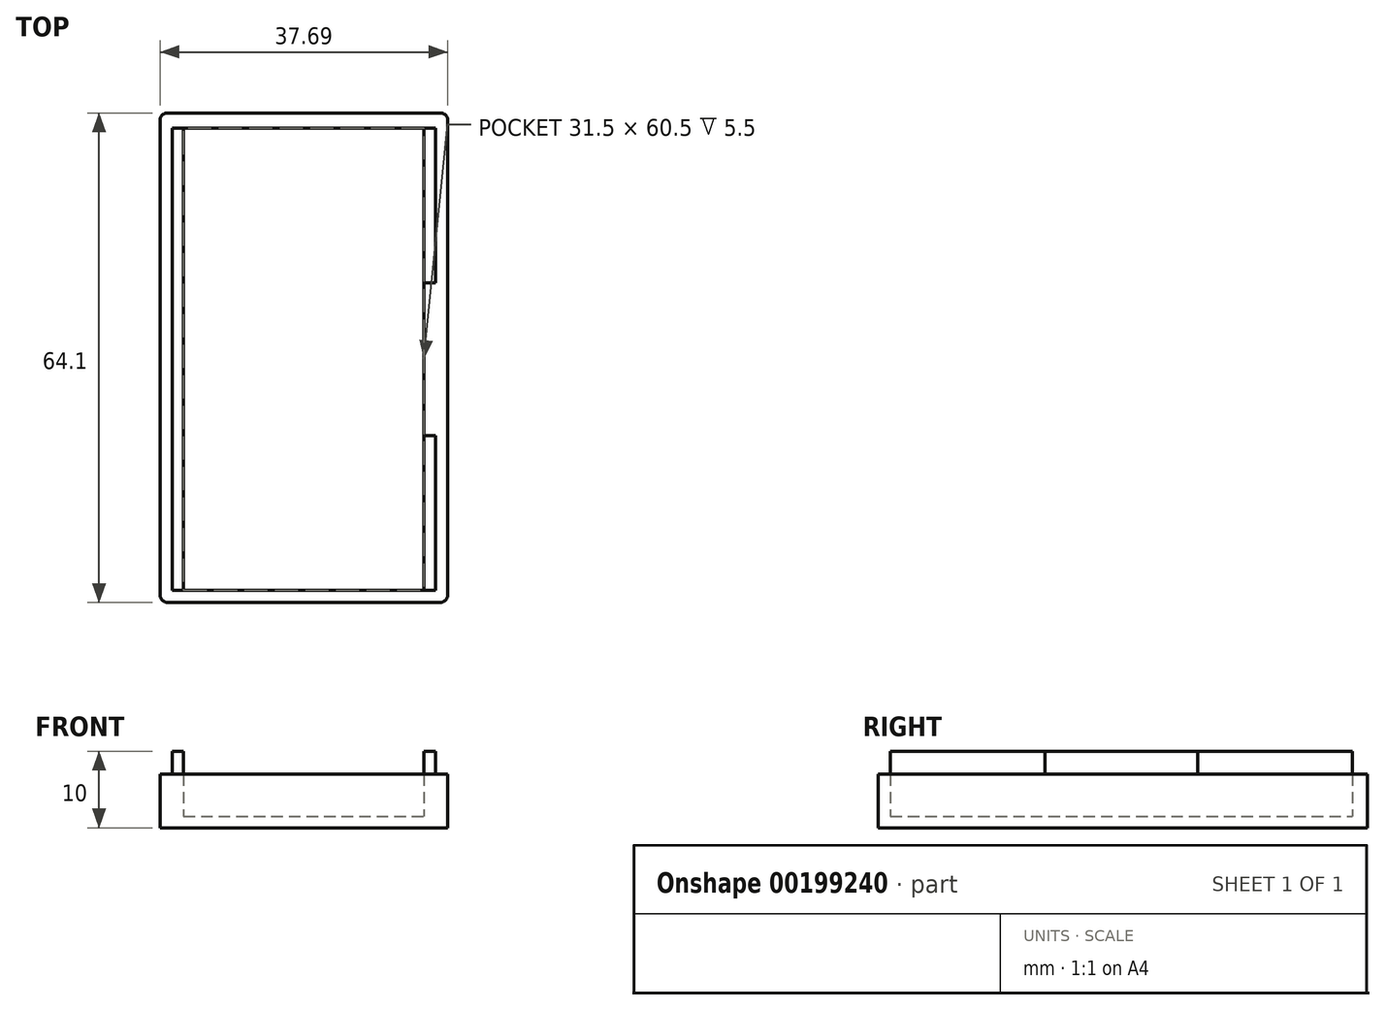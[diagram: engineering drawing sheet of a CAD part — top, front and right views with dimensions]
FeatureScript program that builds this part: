
annotation { "Feature Type Name" : "Feature", "Feature Type Description" : "" }
export const myFeature = defineFeature(function(context is Context, id is Id, definition is map)
    precondition{}
    {
        {
            var Q0;
            Q0=qCreatedBy(makeId("Top.planeOp"),FACE);
            var sketch = newSketch(context, id + "F0", { "sketchPlane" : qUnion([Q0])});
            skLineSegment(sketch, "E0.0.0", {"start": v(18.85, 32.25) * mm, "end": v(-18.84, 32.25) * mm});
            skLineSegment(sketch, "E0.0.1", {"start": v(-18.84, 32.25) * mm, "end": v(-18.84, -31.85) * mm});
            skLineSegment(sketch, "E0.0.2", {"start": v(-18.84, -31.85) * mm, "end": v(18.85, -31.85) * mm});
            skLineSegment(sketch, "E0.0.3", {"start": v(18.85, -31.85) * mm, "end": v(18.85, 32.25) * mm});
            skLineSegment(sketch, "E1.0", {"start": v(-15.75, 30.25) * mm, "end": v(15.75, 30.25) * mm});
            skLineSegment(sketch, "E2.0", {"start": v(-15.75, -30.25) * mm, "end": v(-15.75, 30.25) * mm});
            skLineSegment(sketch, "E3.0", {"start": v(15.75, -30.25) * mm, "end": v(15.75, 30.25) * mm});
            skLineSegment(sketch, "E4.0", {"start": v(-15.75, -30.25) * mm, "end": v(15.75, -30.25) * mm});
            skPoint(sketch, "E5", {"position": v(0, 0) * mm});
            skPoint(sketch, "E5.positionSnap0", {"position": v(0, -30.25) * mm});
            skPoint(sketch, "E6.positionSnap0", {"position": v(15.75, 0) * mm});
            skSolve(sketch);
        }
        {
            var Q0;
            Q0 = qSketchRegion(id + "F0", true);
            extrude(context, id + "F1", {"entities" : qUnion([Q0]), "depth" : 7 * mm});
        }
        {
            var Q0;
            Q0=makeQuery(id+"F0.imprint","IMPRINT",FACE,{"disambiguationData":[TD([[makeQuery(id+"F0.imprint","IMPRINT",EDGE,{"derivedFrom":sQuery(id+"F0.wireOp",EDGE,"E1.0")}),-1.0]])]});
            extrude(context, id + "F2", {"entities" : qUnion([Q0]), "operationType" : NewBodyOperationType.ADD, "depth" : 1.5 * mm});
        }
        {
            var Q0;
            Q0=makeQuery(id+"F1.opExtrude","CAP_FACE",FACE,{"disambiguationData":[OSD([sQuery(id+"F0.wireOp",EDGE,"E0.0.0"),sQuery(id+"F0.wireOp",EDGE,"E0.0.1"),sQuery(id+"F0.wireOp",EDGE,"E0.0.2"),sQuery(id+"F0.wireOp",EDGE,"E0.0.3"),sQuery(id+"F0.wireOp",EDGE,"E1.0"),sQuery(id+"F0.wireOp",EDGE,"E2.0"),sQuery(id+"F0.wireOp",EDGE,"E3.0"),sQuery(id+"F0.wireOp",EDGE,"E4.0")])],"isStart":false});
            var sketch = newSketch(context, id + "F3", { "sketchPlane" : qUnion([Q0])});
            skLineSegment(sketch, "E7.0", {"start": v(-15.75, -30.25) * mm, "end": v(-15.75, 30.25) * mm});
            skLineSegment(sketch, "E8.0", {"start": v(15.75, -30.25) * mm, "end": v(15.75, 30.25) * mm});
            skLineSegment(sketch, "E9", {"start": v(-15.75, 30.25) * mm, "end": v(-17.25, 30.25) * mm});
            skLineSegment(sketch, "E10", {"start": v(-17.25, 30.25) * mm, "end": v(-17.25, -30.25) * mm});
            skLineSegment(sketch, "E11", {"start": v(-17.25, -30.25) * mm, "end": v(-15.75, -30.25) * mm});
            skLineSegment(sketch, "E12", {"start": v(15.75, -30.25) * mm, "end": v(17.25, -30.25) * mm});
            skLineSegment(sketch, "E13", {"start": v(17.25, -30.25) * mm, "end": v(17.25, 30.25) * mm});
            skLineSegment(sketch, "E14", {"start": v(17.25, 30.25) * mm, "end": v(15.75, 30.25) * mm});
            skSolve(sketch);
        }
        {
            var Q0;
            Q0 = qSketchRegion(id + "F3", true);
            extrude(context, id + "F4", {"entities" : qUnion([Q0]), "operationType" : NewBodyOperationType.ADD, "depth" : 3 * mm});
        }
        {
            var Q0;
            Q0=makeQuery(id+"F1.opExtrude","SWEPT_EDGE",EDGE,{"disambiguationData":[OSD([sQuery(id+"F0.wireOp",EDGE,"E0.0.1"),sQuery(id+"F0.wireOp",EDGE,"E0.0.2")])]});
            var Q1;
            Q1=makeQuery(id+"F1.opExtrude","SWEPT_EDGE",EDGE,{"disambiguationData":[OSD([sQuery(id+"F0.wireOp",EDGE,"E0.0.2"),sQuery(id+"F0.wireOp",EDGE,"E0.0.3")])]});
            var Q2;
            Q2=makeQuery(id+"F1.opExtrude","SWEPT_EDGE",EDGE,{"disambiguationData":[OSD([sQuery(id+"F0.wireOp",EDGE,"E0.0.0"),sQuery(id+"F0.wireOp",EDGE,"E0.0.3")])]});
            var Q3;
            Q3=makeQuery(id+"F1.opExtrude","SWEPT_EDGE",EDGE,{"disambiguationData":[OSD([sQuery(id+"F0.wireOp",EDGE,"E0.0.0"),sQuery(id+"F0.wireOp",EDGE,"E0.0.1")])]});
            fillet(context, id + "F5", {"entities" : qUnion([Q0, Q1, Q2, Q3]), "radius" : 1 * mm, "tangentPropagation" : true, "allowEdgeOverflow" : false});
        }
        {
            var Q0;
            Q0=makeQuery(id+"F4.opExtrude","SWEPT_FACE",FACE,{"disambiguationData":[OSD([sQuery(id+"F3.wireOp",EDGE,"E13")])]});
            var sketch = newSketch(context, id + "F6", { "sketchPlane" : qUnion([Q0])});
            skLineSegment(sketch, "E15.bottom", {"start": v(10, 7) * mm, "end": v(-10, 7) * mm});
            skLineSegment(sketch, "E15.top", {"start": v(10, 10) * mm, "end": v(-10, 10) * mm});
            skLineSegment(sketch, "E15.left", {"start": v(10, 7) * mm, "end": v(10, 10) * mm});
            skLineSegment(sketch, "E15.right", {"start": v(-10, 7) * mm, "end": v(-10, 10) * mm});
            skPoint(sketch, "E16", {"position": v(0, 7) * mm});
            skSolve(sketch);
        }
        {
            var Q0;
            Q0 = qSketchRegion(id + "F6", true);
            var Q1;
            Q1=makeQuery(id+"F4.boolean.opBoolean","MERGE",FACE,{"derivedFrom":[makeQuery(id+"F1.opExtrude","SWEPT_FACE",FACE,{"disambiguationData":[OSD([sQuery(id+"F0.wireOp",EDGE,"E3.0")])]}),makeQuery(id+"F4.opExtrude","SWEPT_FACE",FACE,{"disambiguationData":[OSD([sQuery(id+"F3.wireOp",EDGE,"E8.0")])]})]});
            extrude(context, id + "F7", {"entities" : qUnion([Q0]), "operationType" : NewBodyOperationType.REMOVE, "endBound" : BoundingType.UP_TO_SURFACE, "oppositeDirection" : true, "endBoundEntityFace" : qUnion([Q1]), "depth" : 25 * mm});
        }
    });
